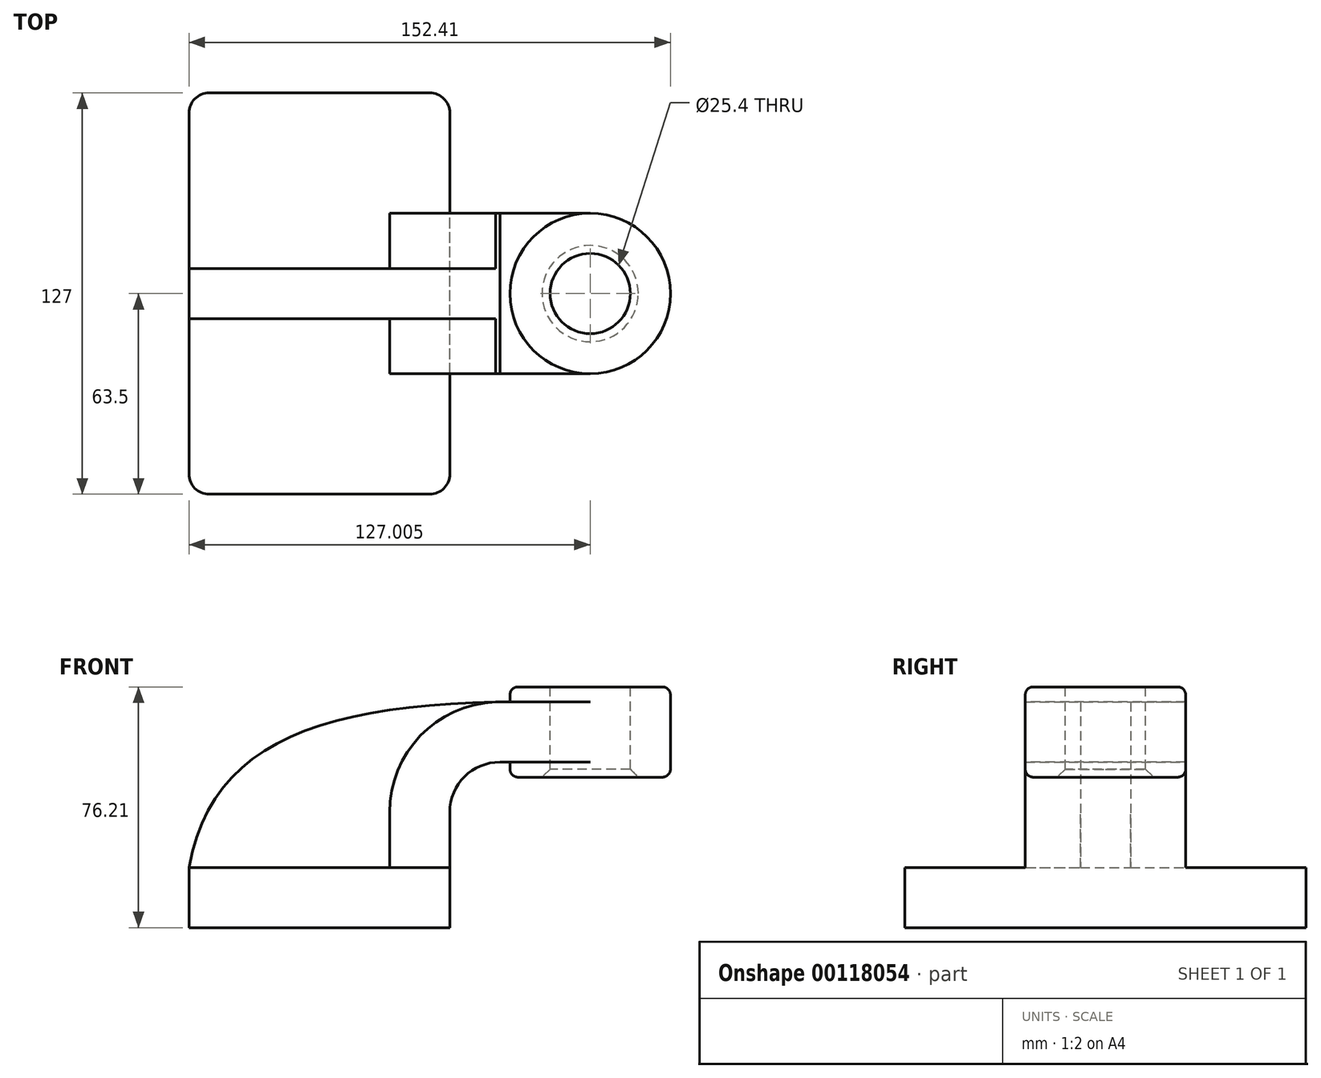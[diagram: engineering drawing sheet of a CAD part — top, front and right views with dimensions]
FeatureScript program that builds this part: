
annotation { "Feature Type Name" : "Feature", "Feature Type Description" : "" }
export const myFeature = defineFeature(function(context is Context, id is Id, definition is map)
    precondition{}
    {
        {
            var Q0;
            Q0=qCreatedBy(makeId("Front.planeOp"),FACE);
            var sketch = newSketch(context, id + "F0", { "sketchPlane" : qUnion([Q0])});
            skLineSegment(sketch, "E0.bottom", {"start": v(41.28, -9.52) * mm, "end": v(-41.28, -9.53) * mm});
            skLineSegment(sketch, "E0.top", {"start": v(41.28, 9.53) * mm, "end": v(-41.28, 9.53) * mm});
            skLineSegment(sketch, "E0.left", {"start": v(41.28, -9.52) * mm, "end": v(41.28, 9.53) * mm});
            skLineSegment(sketch, "E0.right", {"start": v(-41.28, -9.53) * mm, "end": v(-41.28, 9.53) * mm});
            skPoint(sketch, "E0.middle", {"position": v(0, 0) * mm});
            skLineSegment(sketch, "E1.bottom", {"start": v(111.12, 38.1) * mm, "end": v(60.32, 38.1) * mm});
            skLineSegment(sketch, "E1.top", {"start": v(111.12, 66.68) * mm, "end": v(60.32, 66.68) * mm});
            skLineSegment(sketch, "E1.left", {"start": v(111.12, 38.1) * mm, "end": v(111.12, 66.68) * mm});
            skLineSegment(sketch, "E1.right", {"start": v(60.32, 38.1) * mm, "end": v(60.32, 66.67) * mm});
            skPoint(sketch, "E1.middle", {"position": v(85.72, 52.39) * mm});
            skLineSegment(sketch, "E2", {"start": v(41.28, 9.53) * mm, "end": v(41.28, 27) * mm});
            skArc(sketch, "E3", {"start": v(41.27, 27) * mm, "mid": v(45.92, 38.23) * mm, "end": v(57.15, 42.88) * mm});
            skLineSegment(sketch, "E4", {"start": v(57.15, 42.88) * mm, "end": v(85.72, 42.88) * mm});
            skLineSegment(sketch, "E5.0", {"start": v(57.15, 61.93) * mm, "end": v(85.73, 61.93) * mm});
            skArc(sketch, "E5.1", {"start": v(22.23, 27) * mm, "mid": v(32.45, 51.7) * mm, "end": v(57.15, 61.93) * mm});
            skLineSegment(sketch, "E5.2", {"start": v(22.23, 9.53) * mm, "end": v(22.23, 27) * mm});
            skFitSpline(sketch, "E6", {"points": [v(57.15, 61.93) * mm, v(-41.28, 9.53) * mm], "startDerivative": vector(-171.45, -3.17) * mm, "endDerivative": vector(-20.5, -117.7) * mm});
            skLineSegment(sketch, "E7", {"start": v(85.72, 38.1) * mm, "end": v(85.72, 66.68) * mm});
            skSolve(sketch);
        }
        {
            var Q0;
            Q0=makeQuery(id+"F0.imprint","IMPRINT",FACE,{"disambiguationData":[TD([[makeQuery(id+"F0.imprint","IMPRINT",EDGE,{"derivedFrom":sQuery(id+"F0.wireOp",EDGE,"E0.bottom")}),-1.0]])]});
            extrude(context, id + "F1", {"entities" : qUnion([Q0]), "endBound" : BoundingType.SYMMETRIC, "depth" : 127 * mm});
        }
        {
            var Q0;
            {var subQ1=sQuery(id+"F0.wireOp",EDGE,"E2");Q0=makeQuery(id+"F0.imprint","IMPRINT",FACE,{"disambiguationData":[TD([[makeQuery(id+"F0.imprint","IMPRINT",EDGE,{"derivedFrom":subQ1}),1.0]])]});}
            var Q1;
            {var subQ0=sQuery(id+"F0.wireOp",EDGE,"E4");var subQ1=sQuery(id+"F0.wireOp",EDGE,"E1.right");var subQ2=makeQuery(id+"F0.imprint","INTERSECT",VERTEX,{"derivedFrom":[subQ1,subQ0]});Q1=makeQuery(id+"F0.imprint","IMPRINT",FACE,{"disambiguationData":[TD([[makeQuery(id+"F0.imprint","IMPRINT",EDGE,{"disambiguationData":[TD([[subQ2,-1.0]])],"derivedFrom":subQ1}),-1.0]])]});}
            extrude(context, id + "F2", {"entities" : qUnion([Q0, Q1]), "operationType" : NewBodyOperationType.ADD, "endBound" : BoundingType.SYMMETRIC, "depth" : 50.8 * mm});
        }
        {
            var Q0;
            {var subQ3=sQuery(id+"F0.wireOp",EDGE,"E5.2");Q0=makeQuery(id+"F0.imprint","IMPRINT",FACE,{"disambiguationData":[TD([[makeQuery(id+"F0.imprint","IMPRINT",EDGE,{"derivedFrom":subQ3}),1.0]])]});}
            extrude(context, id + "F3", {"entities" : qUnion([Q0]), "operationType" : NewBodyOperationType.ADD, "endBound" : BoundingType.SYMMETRIC, "depth" : 15.88 * mm});
        }
        {
            var Q0;
            {var subQ4=sQuery(id+"F0.wireOp",EDGE,"E1.left");Q0=makeQuery(id+"F0.imprint","IMPRINT",FACE,{"disambiguationData":[TD([[makeQuery(id+"F0.imprint","IMPRINT",EDGE,{"derivedFrom":subQ4}),1.0]])]});}
            var Q1;
            Q1=sQuery(id+"F0.wireOp",EDGE,"E7");
            revolve(context, id + "F4", {"operationType" : NewBodyOperationType.ADD, "entities" : qUnion([Q0]), "axis" : qUnion([Q1]), "revolveType" : RevolveType.FULL});
        }
        {
            var Q0;
            Q0=makeQuery(id+"F1.opExtrude","CAP_EDGE",EDGE,{"disambiguationData":[OSD([sQuery(id+"F0.wireOp",EDGE,"E0.right")])],"isStart":false});
            var Q1;
            Q1=makeQuery(id+"F1.opExtrude","CAP_EDGE",EDGE,{"disambiguationData":[OSD([sQuery(id+"F0.wireOp",EDGE,"E0.left")])],"isStart":false});
            var Q2;
            Q2=makeQuery(id+"F1.opExtrude","CAP_EDGE",EDGE,{"disambiguationData":[OSD([sQuery(id+"F0.wireOp",EDGE,"E0.left")])],"isStart":true});
            var Q3;
            Q3=makeQuery(id+"F1.opExtrude","CAP_EDGE",EDGE,{"disambiguationData":[OSD([sQuery(id+"F0.wireOp",EDGE,"E0.right")])],"isStart":true});
            fillet(context, id + "F5", {"entities" : qUnion([Q0, Q1, Q2, Q3]), "radius" : 6.35 * mm, "tangentPropagation" : true, "allowEdgeOverflow" : false});
        }
        {
            var Q0;
            Q0=makeQuery(id+"F4.opRevolve","SWEPT_FACE",FACE,{"disambiguationData":[OSD([sQuery(id+"F0.wireOp",EDGE,"E1.top")])]});
            var sketch = newSketch(context, id + "F6", { "sketchPlane" : qUnion([Q0])});
            skCircle(sketch, "E8", {"center": v(85.72, 0) * mm, "radius": 12.7 * mm});
            skSolve(sketch);
        }
        {
            var Q0;
            Q0=makeQuery(id+"F6.imprint","IMPRINT",FACE,{"disambiguationData":[TD([[makeQuery(id+"F6.imprint","IMPRINT",EDGE,{"derivedFrom":sQuery(id+"F6.wireOp",EDGE,"E8")}),1.0]])]});
            extrude(context, id + "F7", {"entities" : qUnion([Q0]), "operationType" : NewBodyOperationType.REMOVE, "endBound" : BoundingType.THROUGH_ALL, "oppositeDirection" : true, "depth" : 25.4 * mm});
        }
        {
            var Q0;
            Q0=makeQuery(id+"F4.opRevolve","SWEPT_EDGE",EDGE,{"disambiguationData":[OSD([sQuery(id+"F0.wireOp",EDGE,"E1.top"),sQuery(id+"F0.wireOp",EDGE,"E1.left")])]});
            var Q1;
            Q1=makeQuery(id+"F4.opRevolve","SWEPT_EDGE",EDGE,{"disambiguationData":[OSD([sQuery(id+"F0.wireOp",EDGE,"E1.bottom"),sQuery(id+"F0.wireOp",EDGE,"E1.left")])]});
            fillet(context, id + "F8", {"entities" : qUnion([Q0, Q1]), "radius" : 2.54 * mm, "tangentPropagation" : true, "allowEdgeOverflow" : false});
        }
        {
            var Q0;
            Q0=makeQuery(id+"F7.boolean.opBoolean","COPY",EDGE,{"derivedFrom":makeQuery(id+"F7.opExtrude","CAP_EDGE",EDGE,{"disambiguationData":[OSD([sQuery(id+"F6.wireOp",EDGE,"E8")])],"isStart":true})});
            var Q1;
            Q1=makeQuery(id+"F7.boolean.opBoolean","INTERSECT",EDGE,{"derivedFrom":[makeQuery(id+"F4.opRevolve","SWEPT_FACE",FACE,{"disambiguationData":[OSD([sQuery(id+"F0.wireOp",EDGE,"E1.bottom")])]}),makeQuery(id+"F7.opExtrude","SWEPT_FACE",FACE,{"disambiguationData":[OSD([sQuery(id+"F6.wireOp",EDGE,"E8")])]})]});
            chamfer(context, id + "F9", {"entities" : qUnion([Q0, Q1]), "width" : 2.54 * mm, "tangentPropagation" : true});
        }
    });
